# Revit family: Einbaugeräte_Modul_45-Systeme_Steckdose_0°_Schutzkontakt_2_fach
name_source: partatom
category: Generic Models
revit_build: Autodesk Revit 2015 (Build: 20140606_1530(x64)
units: mm (PartAtom-declared; Revit-internal decimal feet)

## types (6) — shared parameters
Manufacturer = OBO Bettermann
URL = http://www.obo-bettermann.com

## per-type parameters (varying)
| type | GTIN | Manufacturer Art. No. | Material |
| STD-D0 MZGN2 | 4012196047147 | 6120026 | Polycarbonate, minzgrün |
| STD-D0 ROR2 | 4012196047130 | 6120024 | Polycarbonate, reinorange |
| STD-D0 RW2 | 4012196047109 | 6120022 | Polycarbonate, Clear reinweiß |
| STD-D0 SRO2 | 4012196047154 | 6120028 | Polycarbonate, signalrot |
| STD-D0 AL2 | 4012196047222 | 6120032 | Polycarbonate,Alu lackiert |
| STD-D0 SWGR2 | 4012196047208 | 6120030 | Polycarbonate, schwarzgrau |

note: column(s) folded — value = type name in every type: Article Type

## geometry (parser evidence)
native form markers: Sweep x2
no freeform markers — native parametric forms only
